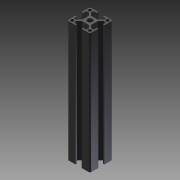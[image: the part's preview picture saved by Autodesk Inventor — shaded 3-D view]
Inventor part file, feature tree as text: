
AUTODESK INVENTOR PART (.ipt)
format: ipt  version: 2011 SP1 (Build 150282100, 282)  size: 189,952 bytes
history: native  units: mm
features: other x21, sketch x3, hole x2, extrude x1, pattern_linear x1
ambient origin geometry x8: Origin, YZ Plane, XZ Plane, XY Plane, X Axis, Y Axis, Z Axis, Center Point
bodies: Solid1 (feature_tree)
feature tree (28):
  extrude  "Extrusion1"  Depth=20.0mm
  hole  "Hole1"  [1 undecoded]
  hole  "Hole2"  [1 undecoded]
  pattern_linear  "Rectangular Pattern1"  [2 undecoded]
  other  "C1_XY"
  other  "C1_YZ"
  other  "C1_ZX"
  other  "C1_X"
  other  "C1_Y"
  other  "C1_Z"
  other  "C1_Center"
  other  "to_frame_cap1_XY"
  other  "to_frame_cap1_YZ"
  other  "to_frame_cap1_ZX"
  other  "to_frame_cap1_X"
  other  "to_frame_cap1_Y"
  other  "to_frame_cap1_Z"
  other  "to_frame_cap1_Center"
  other  "to_frame_cap2_XY"
  other  "to_frame_cap2_YZ"
  other  "to_frame_cap2_ZX"
  other  "to_frame_cap2_X"
  other  "to_frame_cap2_Y"
  other  "to_frame_cap2_Z"
  other  "to_frame_cap2_Center"
  sketch  "Sketch_1"  dims[d0=159.0mm d1=0.0mm]
  sketch  "Sketch2"  dims[d2=6.8mm d3=6.0mm d4=4.0mm d5=2.0mm d6=90.0deg d7=159.0mm d8=0.0mm]
  sketch  "Sketch3"  dims[d9=4.2mm d10=6.0mm d11=4.0mm d12=2.0mm d13=90.0deg d14=159.0mm d15=0.0mm d16=20.0mm d18=23.2mm d19=20.0mm d21=23.2mm d22=0.0mm d23=0.0mm d24=0.0mm]
note: 4 required parameter values undecoded (feature->parameter linkage not recoverable at this tier; creation-order binding heuristic only, values carry confidence <= 0.55)
